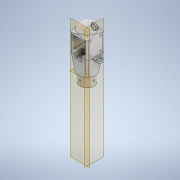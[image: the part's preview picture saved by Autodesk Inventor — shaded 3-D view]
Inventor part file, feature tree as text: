
AUTODESK INVENTOR PART (.ipt)
format: ipt  version: 2022.3 (Build 263350000, 350)  size: 737,792 bytes
history: native  units: mm
features: sketch x21, extrude x16, thicken_offset x7, fillet x5, plane x4, hole x4, mirror x3, revolve x2, projected_geometry x2, loft x1, other x1
ambient origin geometry x8: Origin, YZ Plane, XZ Plane, XY Plane, X Axis, Y Axis, Z Axis, Center Point
bodies: Solid1 (feature_tree)
feature tree (66):
  extrude  "Extrusion1"  Depth=4.0mm
  revolve  "Revolution1"  [1 undecoded]
  plane  "Work Plane1"
  extrude  "Extrusion2"  Depth=100.0mm
  extrude  "Extrusion3"  Depth=150.0mm
  plane  "Work Plane2"
  sketch  "Sketch5"  dims[d12=100.0mm d13=90.0deg]
  fillet  "Fillet1"  Radius=4.0mm
  loft  "Loft1"
  extrude  "Extrusion4"  Depth=5.0mm
  sketch  "Sketch11"  dims[d16=65.0mm d17=65.0mm]
  extrude  "Extrusion7"  Depth=65.0mm
  extrude  "Extrusion8"  Depth=15.0mm
  extrude  "Extrusion9"  Depth=10.0mm TaperAngle=0.0deg
  hole  "Hole2"  [1 undecoded]
  extrude  "Extrusion10"  Depth=50.0mm
  revolve  "Revolution2"  Angle=90.0deg
  fillet  "Fillet3"  [1 undecoded]
  extrude  "Extrusion14"  Depth=5.0mm
  sketch  "Sketch22"  dims[d33=100.0mm d34=0.0mm d54=5.0mm]
  extrude  "Extrusion15"  Depth=5.0mm TaperAngle=0.0deg
  extrude  "Extrusion16"  Depth=45.0mm
  plane  "Work Plane3"
  plane  "Work Plane4"
  sketch  "Sketch23"  dims[d55=4.5mm d56=5.0mm d57=0.0mm]
  sketch  "Sketch24"  dims[d58=48.0mm d59=0.0mm d60=45.0mm]
  hole  "Hole5"  [1 undecoded]
  hole  "Hole6"  [1 undecoded]
  mirror  "Mirror1"
  mirror  "Mirror2"
  thicken_offset  "Thicken1"
  thicken_offset  "Thicken2"
  thicken_offset  "Thicken3"
  thicken_offset  "Thicken4"
  thicken_offset  "Thicken5"
  extrude  "Extrusion17"  Depth=2.0mm TaperAngle=0.0deg
  fillet  "Fillet4"  Radius=26.0mm
  extrude  "Extrusion18"  TaperAngle=90.0deg  [1 undecoded]
  sketch  "Sketch27"  dims[d66=3.4mm d67=6.0mm d68=5.9mm d69=2.0mm d70=90.0deg d71=5.0mm d72=0.0mm d73=3.0mm d74=0.0mm d75=26.0mm]
  fillet  "Fillet5"  Radius=10.0mm
  thicken_offset  "Thicken6"
  extrude  "Extrusion20"  Depth=10.0mm TaperAngle=0.0deg
  fillet  "Fillet6"  Radius=30.0mm
  extrude  "Extrusion21"  Depth=2.0mm TaperAngle=0.0deg
  thicken_offset  "Thicken7"
  hole  "Hole7"  [1 undecoded]
  mirror  "Mirror3"
  extrude  "Extrusion22"  Depth=2.0mm
  sketch  "Sketch1"  dims[d0=80.0mm d1=4.0mm]
  sketch  "Sketch2"  dims[d2=40.0mm d3=0.0mm d4=88.0mm]
  sketch  "Sketch3"  dims[d5=50.0mm d8=100.0mm]
  sketch  "Sketch4"  dims[d9=25.0mm d10=150.0mm d11=4.0mm]
  other  "Edges1"
  sketch  "Sketch7"  dims[d14=-52.5mm d15=5.0mm]
  projected_geometry  "Projected Loop2"
  sketch  "Sketch12"  dims[d18=5.0mm d19=15.0mm]
  sketch  "Sketch13"  dims[d20=10.0mm d21=5.0mm d22=0.0mm]
  sketch  "Sketch14"  dims[d23=52.0mm d24=52.0mm]
  sketch  "Sketch15"  dims[d25=5.0mm d26=0.0mm d27=50.0mm]
  sketch  "Sketch21"  dims[d28=5.0mm d29=0.0mm d30=90.0deg d31=0.0mm d32=90.0deg]
  sketch  "Sketch25"  dims[d61=22.4mm d62=42.0mm d63=0.0mm]
  sketch  "Sketch26"  dims[d64=31.0mm d65=31.0mm]
  projected_geometry  "Projected Loop3"
  sketch  "Sketch29"  dims[d76=26.0mm d77=90.0deg d78=10.0mm]
  sketch  "Sketch30"  dims[d79=0.0mm d143=10.0mm d144=0.0mm d145=30.0mm]
  sketch  "Sketch31"  dims[d146=10.0mm d147=0.0mm d148=30.0mm d149=0.0mm d150=21.0mm d151=21.0mm d152=3.4mm d153=6.0mm d154=4.1mm d155=5.1mm d156=90.0deg d157=1.2mm d158=0.0mm d159=3.4mm d160=6.0mm d161=4.1mm d162=5.1mm d163=90.0deg d164=1.2mm d165=0.0mm d166=42.0mm d167=0.5mm d168=0.5mm d169=0.5mm d170=0.5mm d171=1.0mm d172=1.0mm d173=1.0mm d174=1.0mm d175=1.0mm d176=1.0mm d177=10.0mm d178=10.0mm d179=12.0mm d180=12.0mm d181=14.0mm d182=3.0mm d183=2.5mm d184=2.5mm d185=0.0mm d186=0.0mm d187=2.0mm d188=17.0mm d189=5.0mm d190=21.0mm d191=5.0mm d192=10.0mm d193=10.0mm d194=0.0mm d195=0.0mm d196=20.0mm d197=14.0mm d200=2.0mm d205=18.0mm d206=44.0mm d207=15.0mm d208=10.0mm d209=15.0mm d210=0.0mm d211=2.0mm d212=41.8mm d213=30.0mm d214=0.0mm d215=30.0mm d216=40.0mm d217=3.4mm d218=6.0mm d219=4.1mm d220=5.1mm d221=90.0deg d222=1.2mm d223=0.0mm d224=3.0mm d225=3.0mm d226=0.0mm d227=0.0mm d125=0.872665mm d126=0.872665mm d131=1.0mm d132=1.0mm d133=1.0mm d134=0.15mm d135=0.25mm d136=0.375mm d137=14.3117mm d138=0.75mm d139=20.594885mm d140=0.0625mm d141=0.75mm d142=0.375mm d198=0.5mm d199=0.872665mm d201=0.872665mm d228=0.5mm d229=0.872665mm]
note: 7 required parameter values undecoded (feature->parameter linkage not recoverable at this tier; creation-order binding heuristic only, values carry confidence <= 0.55)